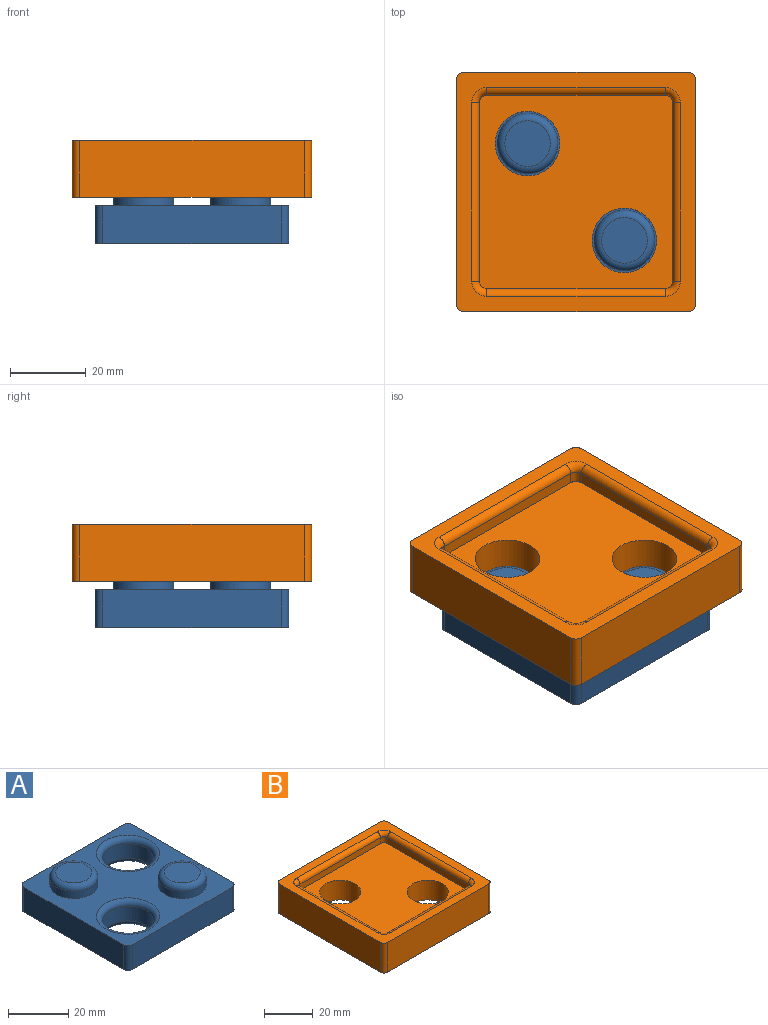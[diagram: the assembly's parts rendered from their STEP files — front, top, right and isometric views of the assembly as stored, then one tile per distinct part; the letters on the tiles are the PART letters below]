
ASSEMBLY  parts=2 mates=1
PART A: 22 faces, bbox 51.3x51.3x15 mm
  f0: cylinder r=8mm len=16mm, axis (0,0,-1), area 150.8mm2, adj f8,f21
  f1: plane 12x12mm, normal (0,0,1), area 113.1mm2, adj f21
  f2: plane 47x10mm, normal (0,1,0), area 470mm2, adj f8,f11,f12,f15
  f3: plane 47x10mm, normal (-1,0,0), area 470mm2, adj f8,f11,f12,f13
  f4: plane 47x10mm, normal (0,-1,0), area 470mm2, adj f8,f11,f13,f14
  f5: cylinder r=8.5mm len=17mm, axis (0,0,-1), area 320.4mm2, adj f17,f19
  f6: cylinder r=8.5mm len=17mm, axis (0,0,-1), area 320.4mm2, adj f16,f18
  f7: plane 47x10mm, normal (1,0,0), area 470mm2, adj f8,f11,f14,f15
  f8: plane 51x51mm, normal (0,0,1), area 1502.7mm2, adj f0,f2,f3,f4,f7,f9,f12,f13
  f9: cylinder r=8mm len=16mm, axis (0,0,-1), area 150.8mm2, adj f8,f20
  f10: plane 12x12mm, normal (0,0,1), area 113.1mm2, adj f20
  f11: plane 51x51mm, normal (0,0,-1), area 1904.8mm2, adj f2,f3,f4,f7,f12,f13,f14,f15
  f12: cylinder r=2mm len=10mm, axis (0,0,1), area 31.4mm2, adj f2,f3,f8,f11
  f13: cylinder r=2mm len=10mm, axis (0,0,-1), area 31.4mm2, adj f3,f4,f8,f11
  f14: cylinder r=2mm len=10mm, axis (0,0,1), area 31.4mm2, adj f4,f7,f8,f11
  f15: cylinder r=2mm len=10mm, axis (0,0,-1), area 31.4mm2, adj f2,f7,f8,f11
  f16: torus R=10.5mm, axis (0,0,1), area 182.1mm2, adj f6,f11
  f17: torus R=10.5mm, axis (0,0,1), area 182.1mm2, adj f5,f11
  f18: torus R=10.5mm, axis (0,0,1), area 182.1mm2, adj f6,f8
  f19: torus R=10.5mm, axis (0,0,1), area 182.1mm2, adj f5,f8
  f20: torus R=6mm, axis (0,0,1), area 143.6mm2, adj f9,f10
  f21: torus R=6mm, axis (0,0,1), area 143.6mm2, adj f0,f1
PART B: 29 faces, bbox 63x63x15 mm
  f0: plane 63x63mm, normal (0,0,1), area 954.3mm2, adj f9,f10,f11,f12,f15,f16,f17,f18
  f1: cylinder r=8.5mm len=17mm, axis (0,0,-1), area 534.1mm2, adj f3,f4
  f2: cylinder r=8.5mm len=17mm, axis (0,0,-1), area 534.1mm2, adj f3,f4
  f3: plane 51x51mm, normal (0,0,1), area 2143.6mm2, adj f1,f2,f5,f6,f7,f8,f13,f14
  f4: plane 63x63mm, normal (0,0,-1), area 3511.6mm2, adj f1,f2,f9,f10,f11,f12,f25,f26
  f5: plane 47x3mm, normal (0,-1,0), area 141mm2, adj f3,f13,f14,f15
  f6: plane 47x3mm, normal (1,0,0), area 141mm2, adj f3,f13,f18,f19
  f7: plane 47x3mm, normal (0,1,0), area 141mm2, adj f3,f19,f20,f24
  f8: plane 47x3mm, normal (-1,0,0), area 141mm2, adj f3,f14,f20,f21
  f9: plane 59x15mm, normal (0,1,0), area 885mm2, adj f0,f4,f25,f28
  f10: plane 59x15mm, normal (-1,0,0), area 885mm2, adj f0,f4,f25,f26
  f11: plane 59x15mm, normal (0,-1,0), area 885mm2, adj f0,f4,f26,f27
  f12: plane 59x15mm, normal (1,0,0), area 885mm2, adj f0,f4,f27,f28
  f13: cylinder r=2mm len=3mm, axis (0,0,-1), area 9.4mm2, adj f3,f5,f6,f16
  f14: cylinder r=2mm len=3mm, axis (0,0,1), area 9.4mm2, adj f3,f5,f8,f17
  f15: cylinder r=2mm len=47mm, axis (-1,0,0), area 147.7mm2, adj f0,f5,f16,f17
  f16: torus R=4mm, axis (0,0,1), area 13.5mm2, adj f0,f13,f15,f18
  f17: torus R=4mm, axis (0,0,1), area 13.5mm2, adj f0,f14,f15,f21
  f18: cylinder r=2mm len=47mm, axis (0,-1,0), area 147.7mm2, adj f0,f6,f16,f22
  f19: cylinder r=2mm len=3mm, axis (0,0,1), area 9.4mm2, adj f3,f6,f7,f22
  f20: cylinder r=2mm len=3mm, axis (0,0,-1), area 9.4mm2, adj f3,f7,f8,f23
  f21: cylinder r=2mm len=47mm, axis (0,1,0), area 147.7mm2, adj f0,f8,f17,f23
  f22: torus R=4mm, axis (0,0,1), area 13.5mm2, adj f0,f18,f19,f24
  f23: torus R=4mm, axis (0,0,1), area 13.5mm2, adj f0,f20,f21,f24
  f24: cylinder r=2mm len=47mm, axis (1,0,0), area 147.7mm2, adj f0,f7,f22,f23
  f25: cylinder r=2mm len=15mm, axis (0,0,1), area 47.1mm2, adj f0,f4,f9,f10
  f26: cylinder r=2mm len=15mm, axis (0,0,-1), area 47.1mm2, adj f0,f4,f10,f11
  f27: cylinder r=2mm len=15mm, axis (0,0,1), area 47.1mm2, adj f0,f4,f11,f12
  f28: cylinder r=2mm len=15mm, axis (0,0,-1), area 47.1mm2, adj f0,f4,f9,f12
PLACE A t=(31.29,9.14,60.96)mm
PLACE B rot(axis=(-0.01,-1,0.08),0deg) t=(-74.98,5.47,73.1)mm
MATE slider A.f9 <-> B.f2  axis (0,0,1) through (44.04,-3.61,75.96)mm
